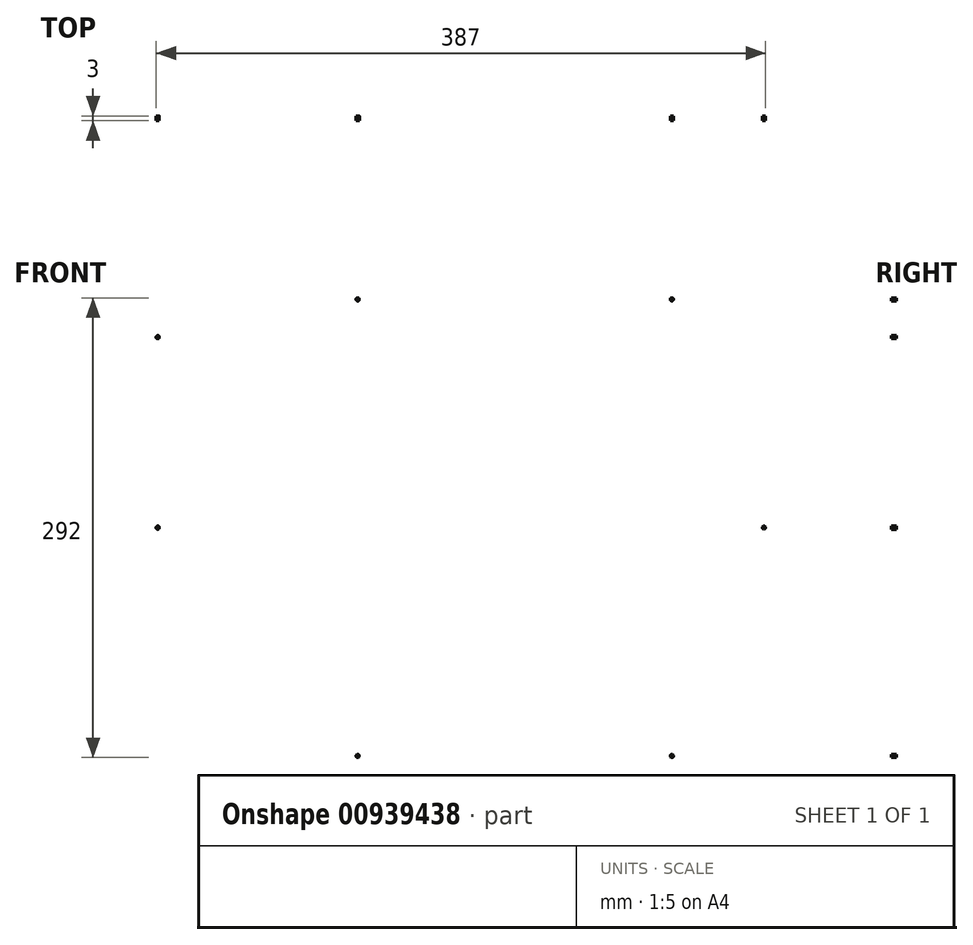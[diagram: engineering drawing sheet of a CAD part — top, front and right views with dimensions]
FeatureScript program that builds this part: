
annotation { "Feature Type Name" : "Feature", "Feature Type Description" : "" }
export const myFeature = defineFeature(function(context is Context, id is Id, definition is map)
    precondition{}
    {
        {
            var Q0;
            Q0=qCreatedBy(makeId("Front.planeOp"),FACE);
            var sketch = newSketch(context, id + "F0", { "sketchPlane" : qUnion([Q0])});
            skLineSegment(sketch, "E0.bottom", {"start": v(-206, 152.5) * mm, "end": v(206, 152.5) * mm});
            skLineSegment(sketch, "E0.top", {"start": v(-206, -152.5) * mm, "end": v(206, -152.5) * mm});
            skLineSegment(sketch, "E0.left", {"start": v(-206, 152.5) * mm, "end": v(-206, -152.5) * mm});
            skLineSegment(sketch, "E0.right", {"start": v(206, 152.5) * mm, "end": v(206, -152.5) * mm});
            skSolve(sketch);
        }
        {
            var Q0;
            Q0 = qSketchRegion(id + "F0", true);
            extrude(context, id + "F1", {"entities" : qUnion([Q0]), "depth" : 3 * mm, "offsetDistance" : 25 * mm});
        }
        {
            var Q0;
            Q0=makeQuery(id+"F1.opExtrude","SWEPT_EDGE",EDGE,{"disambiguationData":[OSD([sQuery(id+"F0.wireOp",EDGE,"E0.bottom"),sQuery(id+"F0.wireOp",EDGE,"E0.left")])]});
            var Q1;
            Q1=makeQuery(id+"F1.opExtrude","SWEPT_EDGE",EDGE,{"disambiguationData":[OSD([sQuery(id+"F0.wireOp",EDGE,"E0.bottom"),sQuery(id+"F0.wireOp",EDGE,"E0.right")])]});
            var Q2;
            Q2=makeQuery(id+"F1.opExtrude","SWEPT_EDGE",EDGE,{"disambiguationData":[OSD([sQuery(id+"F0.wireOp",EDGE,"E0.top"),sQuery(id+"F0.wireOp",EDGE,"E0.left")])]});
            var Q3;
            Q3=makeQuery(id+"F1.opExtrude","SWEPT_EDGE",EDGE,{"disambiguationData":[OSD([sQuery(id+"F0.wireOp",EDGE,"E0.top"),sQuery(id+"F0.wireOp",EDGE,"E0.right")])]});
            fillet(context, id + "F2", {"entities" : qUnion([Q0, Q1, Q2, Q3]), "radius" : 30 * mm, "tangentPropagation" : true, "allowEdgeOverflow" : false});
        }
        {
            var Q0;
            Q0=makeQuery(id+"F1.opExtrude","CAP_FACE",FACE,{"disambiguationData":[OSD([sQuery(id+"F0.wireOp",EDGE,"E0.bottom"),sQuery(id+"F0.wireOp",EDGE,"E0.top"),sQuery(id+"F0.wireOp",EDGE,"E0.left"),sQuery(id+"F0.wireOp",EDGE,"E0.right")])],"isStart":false});
            var sketch = newSketch(context, id + "F3", { "sketchPlane" : qUnion([Q0])});
            skLineSegment(sketch, "E1.bottom", {"start": v(-192.5, 145) * mm, "end": v(192.5, 145) * mm});
            skLineSegment(sketch, "E1.top", {"start": v(-192.5, -145) * mm, "end": v(192.5, -145) * mm});
            skLineSegment(sketch, "E1.left", {"start": v(-192.5, 145) * mm, "end": v(-192.5, -145) * mm});
            skLineSegment(sketch, "E1.right", {"start": v(192.5, 145) * mm, "end": v(192.5, -145) * mm});
            skCircle(sketch, "E2", {"center": v(-192.5, 0) * mm, "radius": 1 * mm});
            skCircle(sketch, "E3", {"center": v(-192.5, 121) * mm, "radius": 1 * mm});
            skCircle(sketch, "E4", {"center": v(-192.5, -121) * mm, "radius": 1 * mm});
            skCircle(sketch, "E5", {"center": v(-65.5, 145) * mm, "radius": 1 * mm});
            skCircle(sketch, "E6", {"center": v(-65.5, -145) * mm, "radius": 1 * mm});
            skCircle(sketch, "E7", {"center": v(192.5, 0) * mm, "radius": 1 * mm});
            skCircle(sketch, "E8", {"center": v(134, 145) * mm, "radius": 1 * mm});
            skCircle(sketch, "E9", {"center": v(134, -145) * mm, "radius": 1 * mm});
            skSolve(sketch);
        }
        {
            var Q0;
            {var subQ0=sQuery(id+"F3.wireOp",EDGE,"E3");var subQ1=sQuery(id+"F3.wireOp",EDGE,"E1.left");var subQ2=makeQuery(id+"F3.imprint","INTERSECT",VERTEX,{"disambiguationData":[OD(0.0)],"derivedFrom":[subQ1,subQ0]});Q0=makeQuery(id+"F3.imprint","IMPRINT",FACE,{"disambiguationData":[TD([[makeQuery(id+"F3.imprint","IMPRINT",EDGE,{"disambiguationData":[TD([[subQ2,-1.0]])],"derivedFrom":subQ1}),-1.0]])]});}
            var Q1;
            {var subQ0=sQuery(id+"F3.wireOp",EDGE,"E3");var subQ1=sQuery(id+"F3.wireOp",EDGE,"E1.left");var subQ2=makeQuery(id+"F3.imprint","INTERSECT",VERTEX,{"disambiguationData":[OD(0.0)],"derivedFrom":[subQ1,subQ0]});Q1=makeQuery(id+"F3.imprint","IMPRINT",FACE,{"disambiguationData":[TD([[makeQuery(id+"F3.imprint","IMPRINT",EDGE,{"disambiguationData":[TD([[subQ2,-1.0]])],"derivedFrom":subQ1}),1.0]])]});}
            var Q2;
            {var subQ0=sQuery(id+"F3.wireOp",EDGE,"E5");var subQ1=sQuery(id+"F3.wireOp",EDGE,"E1.bottom");var subQ2=makeQuery(id+"F3.imprint","INTERSECT",VERTEX,{"disambiguationData":[OD(0.0)],"derivedFrom":[subQ1,subQ0]});Q2=makeQuery(id+"F3.imprint","IMPRINT",FACE,{"disambiguationData":[TD([[makeQuery(id+"F3.imprint","IMPRINT",EDGE,{"disambiguationData":[TD([[subQ2,-1.0]])],"derivedFrom":subQ1}),1.0]])]});}
            var Q3;
            {var subQ0=sQuery(id+"F3.wireOp",EDGE,"E5");var subQ1=sQuery(id+"F3.wireOp",EDGE,"E1.bottom");var subQ2=makeQuery(id+"F3.imprint","INTERSECT",VERTEX,{"disambiguationData":[OD(0.0)],"derivedFrom":[subQ1,subQ0]});Q3=makeQuery(id+"F3.imprint","IMPRINT",FACE,{"disambiguationData":[TD([[makeQuery(id+"F3.imprint","IMPRINT",EDGE,{"disambiguationData":[TD([[subQ2,-1.0]])],"derivedFrom":subQ1}),-1.0]])]});}
            var Q4;
            {var subQ0=sQuery(id+"F3.wireOp",EDGE,"E8");var subQ1=sQuery(id+"F3.wireOp",EDGE,"E1.bottom");var subQ2=makeQuery(id+"F3.imprint","INTERSECT",VERTEX,{"disambiguationData":[OD(0.0)],"derivedFrom":[subQ1,subQ0]});Q4=makeQuery(id+"F3.imprint","IMPRINT",FACE,{"disambiguationData":[TD([[makeQuery(id+"F3.imprint","IMPRINT",EDGE,{"disambiguationData":[TD([[subQ2,-1.0]])],"derivedFrom":subQ1}),1.0]])]});}
            var Q5;
            {var subQ0=sQuery(id+"F3.wireOp",EDGE,"E8");var subQ1=sQuery(id+"F3.wireOp",EDGE,"E1.bottom");var subQ2=makeQuery(id+"F3.imprint","INTERSECT",VERTEX,{"disambiguationData":[OD(0.0)],"derivedFrom":[subQ1,subQ0]});Q5=makeQuery(id+"F3.imprint","IMPRINT",FACE,{"disambiguationData":[TD([[makeQuery(id+"F3.imprint","IMPRINT",EDGE,{"disambiguationData":[TD([[subQ2,-1.0]])],"derivedFrom":subQ1}),-1.0]])]});}
            var Q6;
            {var subQ0=sQuery(id+"F3.wireOp",EDGE,"E7");var subQ1=sQuery(id+"F3.wireOp",EDGE,"E1.right");var subQ2=makeQuery(id+"F3.imprint","INTERSECT",VERTEX,{"disambiguationData":[OD(0.0)],"derivedFrom":[subQ1,subQ0]});Q6=makeQuery(id+"F3.imprint","IMPRINT",FACE,{"disambiguationData":[TD([[makeQuery(id+"F3.imprint","IMPRINT",EDGE,{"disambiguationData":[TD([[subQ2,-1.0]])],"derivedFrom":subQ1}),-1.0]])]});}
            var Q7;
            {var subQ0=sQuery(id+"F3.wireOp",EDGE,"E7");var subQ1=sQuery(id+"F3.wireOp",EDGE,"E1.right");var subQ2=makeQuery(id+"F3.imprint","INTERSECT",VERTEX,{"disambiguationData":[OD(0.0)],"derivedFrom":[subQ1,subQ0]});Q7=makeQuery(id+"F3.imprint","IMPRINT",FACE,{"disambiguationData":[TD([[makeQuery(id+"F3.imprint","IMPRINT",EDGE,{"disambiguationData":[TD([[subQ2,-1.0]])],"derivedFrom":subQ1}),1.0]])]});}
            var Q8;
            {var subQ0=sQuery(id+"F3.wireOp",EDGE,"E9");var subQ1=sQuery(id+"F3.wireOp",EDGE,"E1.top");var subQ2=makeQuery(id+"F3.imprint","INTERSECT",VERTEX,{"disambiguationData":[OD(0.0)],"derivedFrom":[subQ1,subQ0]});Q8=makeQuery(id+"F3.imprint","IMPRINT",FACE,{"disambiguationData":[TD([[makeQuery(id+"F3.imprint","IMPRINT",EDGE,{"disambiguationData":[TD([[subQ2,-1.0]])],"derivedFrom":subQ1}),1.0]])]});}
            var Q9;
            {var subQ0=sQuery(id+"F3.wireOp",EDGE,"E9");var subQ1=sQuery(id+"F3.wireOp",EDGE,"E1.top");var subQ2=makeQuery(id+"F3.imprint","INTERSECT",VERTEX,{"disambiguationData":[OD(0.0)],"derivedFrom":[subQ1,subQ0]});Q9=makeQuery(id+"F3.imprint","IMPRINT",FACE,{"disambiguationData":[TD([[makeQuery(id+"F3.imprint","IMPRINT",EDGE,{"disambiguationData":[TD([[subQ2,-1.0]])],"derivedFrom":subQ1}),-1.0]])]});}
            var Q10;
            {var subQ0=sQuery(id+"F3.wireOp",EDGE,"E6");var subQ1=sQuery(id+"F3.wireOp",EDGE,"E1.top");var subQ2=makeQuery(id+"F3.imprint","INTERSECT",VERTEX,{"disambiguationData":[OD(0.0)],"derivedFrom":[subQ1,subQ0]});Q10=makeQuery(id+"F3.imprint","IMPRINT",FACE,{"disambiguationData":[TD([[makeQuery(id+"F3.imprint","IMPRINT",EDGE,{"disambiguationData":[TD([[subQ2,-1.0]])],"derivedFrom":subQ1}),1.0]])]});}
            var Q11;
            {var subQ0=sQuery(id+"F3.wireOp",EDGE,"E6");var subQ1=sQuery(id+"F3.wireOp",EDGE,"E1.top");var subQ2=makeQuery(id+"F3.imprint","INTERSECT",VERTEX,{"disambiguationData":[OD(0.0)],"derivedFrom":[subQ1,subQ0]});Q11=makeQuery(id+"F3.imprint","IMPRINT",FACE,{"disambiguationData":[TD([[makeQuery(id+"F3.imprint","IMPRINT",EDGE,{"disambiguationData":[TD([[subQ2,-1.0]])],"derivedFrom":subQ1}),-1.0]])]});}
            var Q12;
            {var subQ0=sQuery(id+"F3.wireOp",EDGE,"E4");var subQ1=sQuery(id+"F3.wireOp",EDGE,"E1.left");var subQ2=makeQuery(id+"F3.imprint","INTERSECT",VERTEX,{"disambiguationData":[OD(0.0)],"derivedFrom":[subQ1,subQ0]});Q12=makeQuery(id+"F3.imprint","IMPRINT",FACE,{"disambiguationData":[TD([[makeQuery(id+"F3.imprint","IMPRINT",EDGE,{"disambiguationData":[TD([[subQ2,-1.0]])],"derivedFrom":subQ1}),-1.0]])]});}
            var Q13;
            {var subQ0=sQuery(id+"F3.wireOp",EDGE,"E4");var subQ1=sQuery(id+"F3.wireOp",EDGE,"E1.left");var subQ2=makeQuery(id+"F3.imprint","INTERSECT",VERTEX,{"disambiguationData":[OD(0.0)],"derivedFrom":[subQ1,subQ0]});Q13=makeQuery(id+"F3.imprint","IMPRINT",FACE,{"disambiguationData":[TD([[makeQuery(id+"F3.imprint","IMPRINT",EDGE,{"disambiguationData":[TD([[subQ2,-1.0]])],"derivedFrom":subQ1}),1.0]])]});}
            var Q14;
            {var subQ0=sQuery(id+"F3.wireOp",EDGE,"E2");var subQ1=sQuery(id+"F3.wireOp",EDGE,"E1.left");var subQ2=makeQuery(id+"F3.imprint","INTERSECT",VERTEX,{"disambiguationData":[OD(0.0)],"derivedFrom":[subQ1,subQ0]});Q14=makeQuery(id+"F3.imprint","IMPRINT",FACE,{"disambiguationData":[TD([[makeQuery(id+"F3.imprint","IMPRINT",EDGE,{"disambiguationData":[TD([[subQ2,-1.0]])],"derivedFrom":subQ1}),-1.0]])]});}
            var Q15;
            {var subQ0=sQuery(id+"F3.wireOp",EDGE,"E2");var subQ1=sQuery(id+"F3.wireOp",EDGE,"E1.left");var subQ2=makeQuery(id+"F3.imprint","INTERSECT",VERTEX,{"disambiguationData":[OD(0.0)],"derivedFrom":[subQ1,subQ0]});Q15=makeQuery(id+"F3.imprint","IMPRINT",FACE,{"disambiguationData":[TD([[makeQuery(id+"F3.imprint","IMPRINT",EDGE,{"disambiguationData":[TD([[subQ2,-1.0]])],"derivedFrom":subQ1}),1.0]])]});}
            extrude(context, id + "F4", {"entities" : qUnion([Q0, Q1, Q2, Q3, Q4, Q5, Q6, Q7, Q8, Q9, Q10, Q11, Q12, Q13, Q14, Q15]), "operationType" : NewBodyOperationType.REMOVE, "oppositeDirection" : true, "depth" : 25 * mm, "offsetDistance" : 25 * mm});
        }
    });
